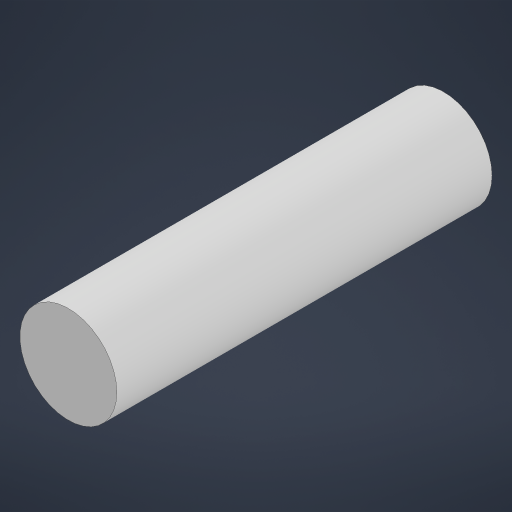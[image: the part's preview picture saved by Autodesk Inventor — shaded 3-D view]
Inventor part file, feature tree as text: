
AUTODESK INVENTOR PART (.ipt)
format: ipt  version: 2024.3 (Build 283343000, 343)  size: 156,160 bytes
history: native  units: mm
features: extrude x1, sketch x1
ambient origin geometry x8: Origin, YZ Plane, XZ Plane, XY Plane, X Axis, Y Axis, Z Axis, Center Point
bodies: Solid1 (feature_tree)
feature tree (2):
  extrude  "Extrusion1"  Depth=11.619mm TaperAngle=0.0deg
  sketch  "Sketch1"  dims[d0=3.0mm d1=11.619mm d2=0.0mm]
